# Revit family: Pultdach_oG_Flachdach_ceiling
name_source: partatom
category: Fenster
units: mm (PartAtom-declared; Revit-internal decimal feet)

## family parameters
Basisbauteil = Geschossdecke
Beim Laden mit Abzugskörper schneiden = Ja
Gemeinsam genutzt = Nein
Immer vertikal = Ja
Raumberechnungspunkt = Nein

## types (1)
- Pultdach_oG_Flachdach_ceiling
    - external length = -7692 mm  [stored -25.2362 ft]
    - inner length = 7500 mm  [stored 24.6063 ft]
    Baugruppenkennzeichen = B3020110
    Breite = 4000 mm  [stored 13.1234 ft]
    Frame Material = Aluminium (1)
    Glazing Material = Glas
    Hersteller = LAMILUX Heinrich Strunz GmbH
    Höhe = 520 mm
    Modell = Glasdach PR60
    Product data url = https://www.bimobject.com
    URL = https://www.lamilux.com
    begin wether sheet = -7547 mm
    construction height = 520 mm
    end wether sheet = -7680 mm  [stored -25.1969 ft]
    external width = 4192 mm  [stored 13.7533 ft]
    glass roof inclination = 3,00°
    inner length = 7500 mm  [stored 24.6063 ft]
    inner width = 4000 mm  [stored 13.1234 ft]
    length wether sheet = -7682 mm  [stored -25.2034 ft]
    lower frame height = 300 mm  [stored 0.984252 ft]
    max. rafter distance = max rafter distance : 1,5 m
    rd = 1570 mm
    rd1 = max rafter distance : 1,0 m
    rd2 = max rafter distance : 1,5 m
    segment distance = 1514 mm
    segment quantity = 5

note: [stored X ft] marks values corroborated as IEEE doubles in the binary element streams (Revit-internal decimal feet)
